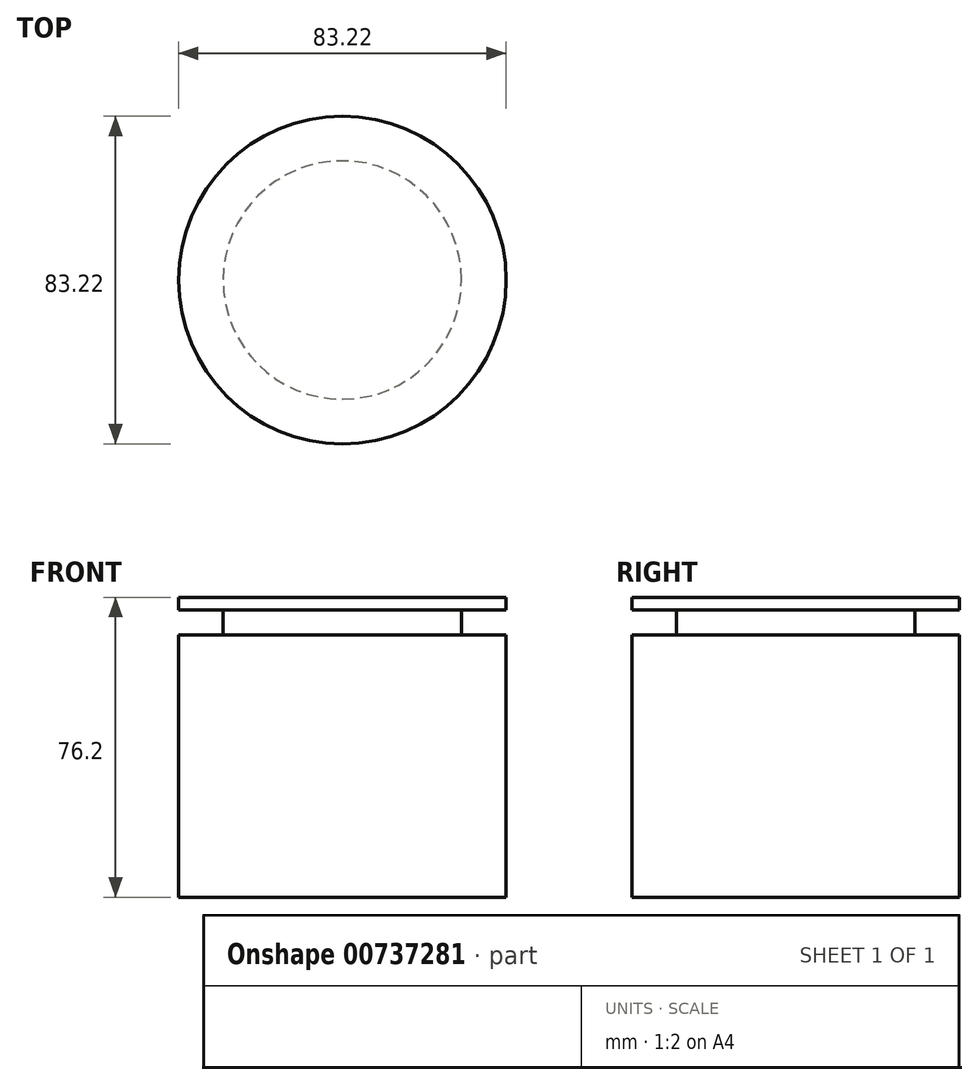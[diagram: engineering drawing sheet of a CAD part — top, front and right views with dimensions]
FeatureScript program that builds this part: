
annotation { "Feature Type Name" : "Feature", "Feature Type Description" : "" }
export const myFeature = defineFeature(function(context is Context, id is Id, definition is map)
    precondition{}
    {
        {
            var Q0;
            Q0=qCreatedBy(makeId("Top.planeOp"),FACE);
            var sketch = newSketch(context, id + "F0", { "sketchPlane" : qUnion([Q0])});
            skCircle(sketch, "E0", {"center": v(0, 0) * mm, "radius": 41.6 * mm});
            skSolve(sketch);
        }
        {
            var Q0;
            Q0=makeQuery(id+"F0.imprint","IMPRINT",FACE,{"disambiguationData":[TD([[makeQuery(id+"F0.imprint","IMPRINT",EDGE,{"derivedFrom":sQuery(id+"F0.wireOp",EDGE,"E0")}),1.0]])]});
            extrude(context, id + "F1", {"entities" : qUnion([Q0]), "depth" : 76.2 * mm, "offsetDistance" : 25.4 * mm});
        }
        {
            var Q0;
            Q0=qCreatedBy(makeId("Right.planeOp"),FACE);
            var sketch = newSketch(context, id + "F2", { "sketchPlane" : qUnion([Q0])});
            skLineSegment(sketch, "E1", {"start": v(0, 75.8) * mm, "end": v(0, 0) * mm});
            skLineSegment(sketch, "E2", {"start": v(30.27, 73) * mm, "end": v(52.74, 73) * mm});
            skLineSegment(sketch, "E3", {"start": v(52.74, 73) * mm, "end": v(52.74, 66.62) * mm});
            skLineSegment(sketch, "E4", {"start": v(52.74, 66.62) * mm, "end": v(30.27, 66.62) * mm});
            skLineSegment(sketch, "E5", {"start": v(30.27, 66.62) * mm, "end": v(30.27, 73) * mm});
            skSolve(sketch);
        }
        {
            var Q0;
            Q0=makeQuery(id+"F2.imprint","IMPRINT",FACE,{"disambiguationData":[TD([[makeQuery(id+"F2.imprint","IMPRINT",EDGE,{"derivedFrom":sQuery(id+"F2.wireOp",EDGE,"E2")}),-1.0]])]});
            var Q1;
            Q1=sQuery(id+"F2.wireOp",EDGE,"E1");
            revolve(context, id + "F3", {"operationType" : NewBodyOperationType.REMOVE, "surfaceOperationType" : NewSurfaceOperationType.NEW, "entities" : qUnion([Q0]), "axis" : qUnion([Q1]), "revolveType" : RevolveType.FULL, "oppositeDirection" : true});
        }
    });
